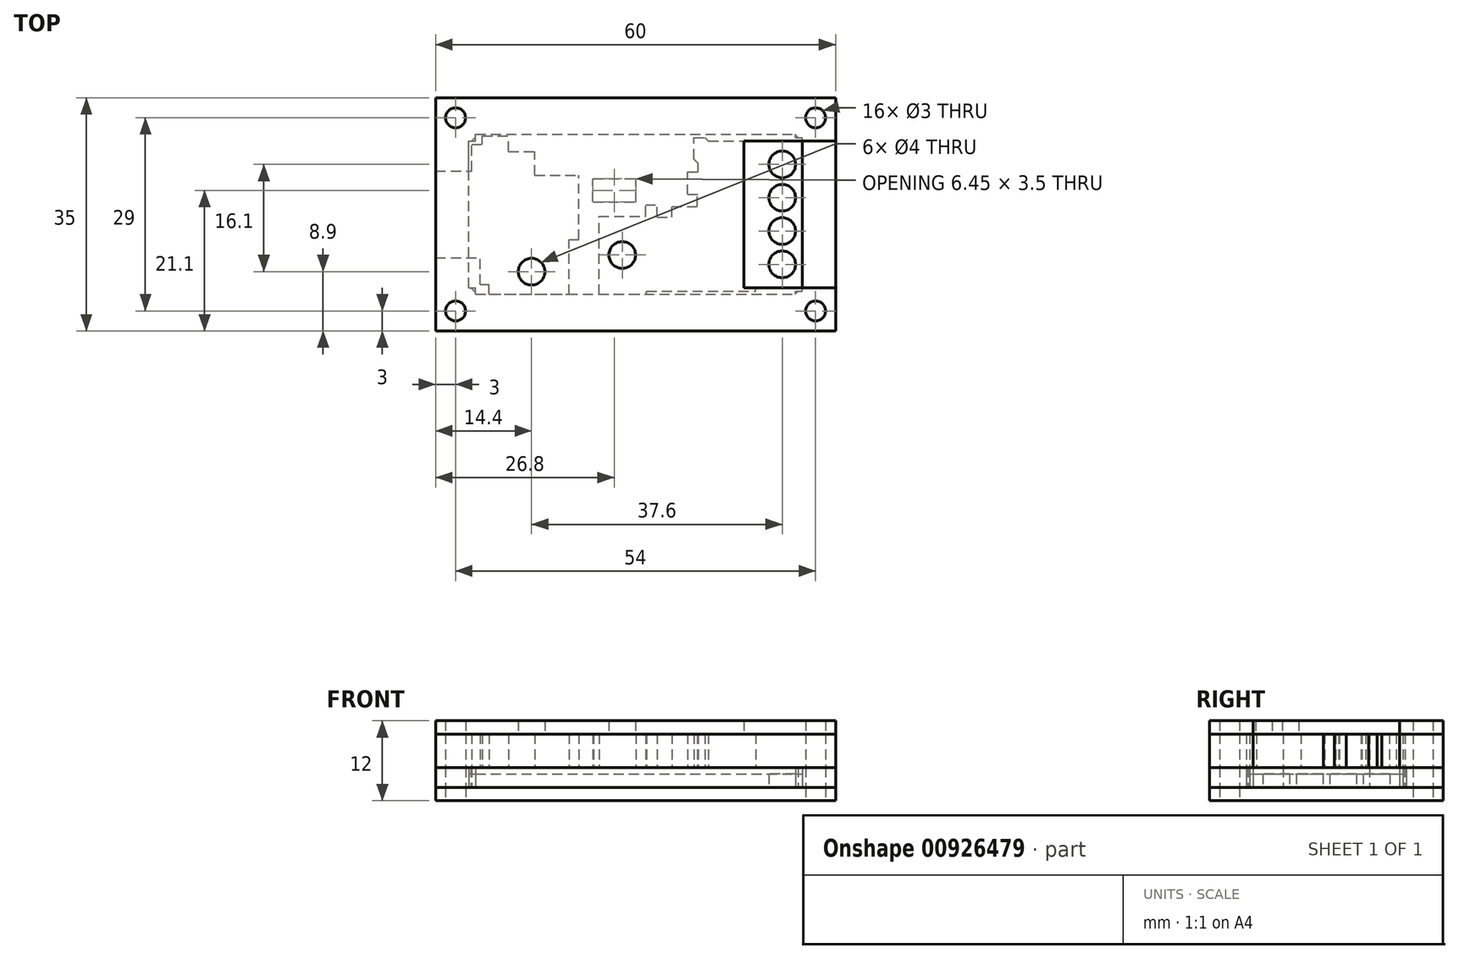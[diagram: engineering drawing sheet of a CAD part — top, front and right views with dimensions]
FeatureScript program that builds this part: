
annotation { "Feature Type Name" : "Feature", "Feature Type Description" : "" }
export const myFeature = defineFeature(function(context is Context, id is Id, definition is map)
    precondition{}
    {
        {
            var Q0;
            Q0=qCreatedBy(makeId("Top.planeOp"),FACE);
            var sketch = newSketch(context, id + "F0", { "sketchPlane" : qUnion([Q0])});
            skLineSegment(sketch, "E0", {"start": v(-30, -17.5) * mm, "end": v(-30, 17.5) * mm});
            skLineSegment(sketch, "E1", {"start": v(-30, 17.5) * mm, "end": v(30, 17.5) * mm});
            skLineSegment(sketch, "E2", {"start": v(30, -17.5) * mm, "end": v(30, 17.5) * mm});
            skLineSegment(sketch, "E3", {"start": v(-30, -17.5) * mm, "end": v(30, -17.5) * mm});
            skCircle(sketch, "E4", {"center": v(-27, -14.5) * mm, "radius": 1.5 * mm});
            skCircle(sketch, "E5", {"center": v(-27, 14.5) * mm, "radius": 1.5 * mm});
            skCircle(sketch, "E6", {"center": v(27, 14.5) * mm, "radius": 1.5 * mm});
            skCircle(sketch, "E7", {"center": v(27, -14.5) * mm, "radius": 1.5 * mm});
            skSolve(sketch);
        }
        {
            var Q0;
            Q0=makeQuery(id+"F0.imprint","IMPRINT",FACE,{"disambiguationData":[TD([[makeQuery(id+"F0.imprint","IMPRINT",EDGE,{"derivedFrom":sQuery(id+"F0.wireOp",EDGE,"E0")}),-1.0]])]});
            extrude(context, id + "F1", {"entities" : qUnion([Q0]), "depth" : 2 * mm, "offsetDistance" : 25 * mm});
        }
        {
            var Q0;
            Q0=makeQuery(id+"F1.opExtrude","CAP_FACE",FACE,{"disambiguationData":[OSD([sQuery(id+"F0.wireOp",EDGE,"E0"),sQuery(id+"F0.wireOp",EDGE,"E1"),sQuery(id+"F0.wireOp",EDGE,"E2"),sQuery(id+"F0.wireOp",EDGE,"E3"),sQuery(id+"F0.wireOp",EDGE,"E4"),sQuery(id+"F0.wireOp",EDGE,"E5"),sQuery(id+"F0.wireOp",EDGE,"E6"),sQuery(id+"F0.wireOp",EDGE,"E7")])],"isStart":false});
            cPlane(context, id + "F2", {"entities" : qUnion([Q0]), "cplaneType" : CPlaneType.OFFSET, "offset" : 0 * mm, "width" : 150 * mm, "height" : 150 * mm});
        }
        {
            var Q0;
            Q0=qCreatedBy(id+"F2.planeOp",FACE);
            var sketch = newSketch(context, id + "F3", { "sketchPlane" : qUnion([Q0])});
            skLineSegment(sketch, "E8", {"start": v(24, -12) * mm, "end": v(24, -11.9) * mm});
            skLineSegment(sketch, "E9", {"start": v(-25, -11) * mm, "end": v(-25, -6.5) * mm});
            skLineSegment(sketch, "E10", {"start": v(-30, -6.5) * mm, "end": v(-25, -6.5) * mm});
            skLineSegment(sketch, "E11", {"start": v(-30, 6.5) * mm, "end": v(-25, 6.5) * mm});
            skLineSegment(sketch, "E12", {"start": v(-25, 6.5) * mm, "end": v(-25, 11) * mm});
            skLineSegment(sketch, "E13", {"start": v(-24, 12) * mm, "end": v(24, 12) * mm});
            skLineSegment(sketch, "E14", {"start": v(25, -11.5) * mm, "end": v(25, 11.5) * mm});
            skLineSegment(sketch, "E15", {"start": v(-24, -12) * mm, "end": v(24, -12) * mm});
            skLineSegment(sketch, "E16", {"start": v(-30, -17.5) * mm, "end": v(-30, -6.5) * mm});
            skLineSegment(sketch, "E17", {"start": v(-30, -17.5) * mm, "end": v(30, -17.5) * mm});
            skLineSegment(sketch, "E18", {"start": v(30, -17.5) * mm, "end": v(30, 11) * mm});
            skLineSegment(sketch, "E19", {"start": v(30, 11) * mm, "end": v(30, 17.5) * mm});
            skLineSegment(sketch, "E20", {"start": v(-30, 17.5) * mm, "end": v(30, 17.5) * mm});
            skLineSegment(sketch, "E21", {"start": v(-30, 6.5) * mm, "end": v(-30, 17.5) * mm});
            skLineSegment(sketch, "E22", {"start": v(-25, 11) * mm, "end": v(-24.6, 11) * mm});
            skLineSegment(sketch, "E23", {"start": v(-24.6, 11) * mm, "end": v(-24, 11.6) * mm});
            skLineSegment(sketch, "E24", {"start": v(-24, 11.6) * mm, "end": v(-24, 12) * mm});
            skLineSegment(sketch, "E25", {"start": v(24.4, 11.5) * mm, "end": v(25, 11.5) * mm});
            skLineSegment(sketch, "E26", {"start": v(24, 11.9) * mm, "end": v(24.4, 11.5) * mm});
            skLineSegment(sketch, "E27", {"start": v(24, 11.9) * mm, "end": v(24, 12) * mm});
            skLineSegment(sketch, "E28", {"start": v(24.4, -11.5) * mm, "end": v(25, -11.5) * mm});
            skLineSegment(sketch, "E29", {"start": v(24, -11.9) * mm, "end": v(24.4, -11.5) * mm});
            skLineSegment(sketch, "E30", {"start": v(-24, -12) * mm, "end": v(-24, -11.7) * mm});
            skLineSegment(sketch, "E31", {"start": v(-24.7, -11) * mm, "end": v(-24, -11.7) * mm});
            skLineSegment(sketch, "E32", {"start": v(-25, -11) * mm, "end": v(-24.7, -11) * mm});
            skCircle(sketch, "E33", {"center": v(-27, -14.5) * mm, "radius": 1.5 * mm});
            skCircle(sketch, "E34", {"center": v(-27, 14.5) * mm, "radius": 1.5 * mm});
            skCircle(sketch, "E35", {"center": v(27, 14.5) * mm, "radius": 1.5 * mm});
            skCircle(sketch, "E36", {"center": v(27, -14.5) * mm, "radius": 1.5 * mm});
            skSolve(sketch);
        }
        {
            var Q0;
            Q0 = qSketchRegion(id + "F3", true);
            extrude(context, id + "F4", {"entities" : qUnion([Q0]), "depth" : 3 * mm, "offsetDistance" : 25 * mm});
        }
        {
            var Q0;
            Q0=qCreatedBy(id+"F2.planeOp",FACE);
            var sketch = newSketch(context, id + "F5", { "sketchPlane" : qUnion([Q0])});
            skLineSegment(sketch, "E37", {"start": v(-24, -12) * mm, "end": v(-24, -11) * mm});
            skLineSegment(sketch, "E38", {"start": v(-25, -11) * mm, "end": v(-24, -11) * mm});
            skLineSegment(sketch, "E39", {"start": v(-25, -11) * mm, "end": v(-25, 11) * mm});
            skLineSegment(sketch, "E40", {"start": v(-24, 12) * mm, "end": v(24, 12) * mm});
            skLineSegment(sketch, "E41", {"start": v(24, 11.5) * mm, "end": v(24, 12) * mm});
            skLineSegment(sketch, "E42", {"start": v(24, 11.5) * mm, "end": v(25, 11.5) * mm});
            skLineSegment(sketch, "E43", {"start": v(25, -11.5) * mm, "end": v(25, 11.5) * mm});
            skLineSegment(sketch, "E44", {"start": v(24, -11.5) * mm, "end": v(25, -11.5) * mm});
            skLineSegment(sketch, "E45", {"start": v(24, -12) * mm, "end": v(24, -11.5) * mm});
            skLineSegment(sketch, "E46", {"start": v(-24, -12) * mm, "end": v(24, -12) * mm});
            skLineSegment(sketch, "E47", {"start": v(-25, 11) * mm, "end": v(-24, 11) * mm});
            skLineSegment(sketch, "E48", {"start": v(-24, 11) * mm, "end": v(-24, 12) * mm});
            skCircle(sketch, "E49", {"center": v(22, 7.5) * mm, "radius": 2 * mm});
            skCircle(sketch, "E50", {"center": v(22, 2.5) * mm, "radius": 2 * mm});
            skCircle(sketch, "E51", {"center": v(22, -2.5) * mm, "radius": 2 * mm});
            skCircle(sketch, "E52", {"center": v(22, -7.5) * mm, "radius": 2 * mm});
            skSolve(sketch);
        }
        {
            var Q0;
            Q0 = qSketchRegion(id + "F5", true);
            extrude(context, id + "F6", {"entities" : qUnion([Q0]), "depth" : 2 * mm, "offsetDistance" : 25 * mm});
        }
        {
            var Q0;
            Q0=makeQuery(id+"F4.opExtrude","CAP_FACE",FACE,{"disambiguationData":[OSD([sQuery(id+"F3.wireOp",EDGE,"E8"),sQuery(id+"F3.wireOp",EDGE,"E9"),sQuery(id+"F3.wireOp",EDGE,"E10"),sQuery(id+"F3.wireOp",EDGE,"E11"),sQuery(id+"F3.wireOp",EDGE,"E12"),sQuery(id+"F3.wireOp",EDGE,"E13"),sQuery(id+"F3.wireOp",EDGE,"E14"),sQuery(id+"F3.wireOp",EDGE,"E15"),sQuery(id+"F3.wireOp",EDGE,"E16"),sQuery(id+"F3.wireOp",EDGE,"E17"),sQuery(id+"F3.wireOp",EDGE,"E18"),sQuery(id+"F3.wireOp",EDGE,"E19"),sQuery(id+"F3.wireOp",EDGE,"E20"),sQuery(id+"F3.wireOp",EDGE,"E21"),sQuery(id+"F3.wireOp",EDGE,"E22"),sQuery(id+"F3.wireOp",EDGE,"E23"),sQuery(id+"F3.wireOp",EDGE,"E24"),sQuery(id+"F3.wireOp",EDGE,"E25"),sQuery(id+"F3.wireOp",EDGE,"E26"),sQuery(id+"F3.wireOp",EDGE,"E27"),sQuery(id+"F3.wireOp",EDGE,"E28"),sQuery(id+"F3.wireOp",EDGE,"E29"),sQuery(id+"F3.wireOp",EDGE,"E30"),sQuery(id+"F3.wireOp",EDGE,"E31"),sQuery(id+"F3.wireOp",EDGE,"E32"),sQuery(id+"F3.wireOp",EDGE,"E33"),sQuery(id+"F3.wireOp",EDGE,"E34"),sQuery(id+"F3.wireOp",EDGE,"E35"),sQuery(id+"F3.wireOp",EDGE,"E36")])],"isStart":false});
            cPlane(context, id + "F7", {"entities" : qUnion([Q0]), "cplaneType" : CPlaneType.OFFSET, "offset" : 0 * mm, "width" : 150 * mm, "height" : 150 * mm});
        }
        {
            var Q0;
            Q0=qCreatedBy(id+"F7.planeOp",FACE);
            var sketch = newSketch(context, id + "F8", { "sketchPlane" : qUnion([Q0])});
            skLineSegment(sketch, "E53", {"start": v(-23, 11.8) * mm, "end": v(-19.05, 11.8) * mm});
            skLineSegment(sketch, "E54", {"start": v(-15.12, 5.9) * mm, "end": v(-8.5, 5.9) * mm});
            skLineSegment(sketch, "E55", {"start": v(-8.5, -1.5) * mm, "end": v(-8.5, 5.9) * mm});
            skLineSegment(sketch, "E56", {"start": v(-30, 6.5) * mm, "end": v(-30, 17.5) * mm});
            skLineSegment(sketch, "E57", {"start": v(-30, 17.5) * mm, "end": v(30, 17.5) * mm});
            skLineSegment(sketch, "E58", {"start": v(30, 11) * mm, "end": v(30, 17.5) * mm});
            skLineSegment(sketch, "E59", {"start": v(30, -17.5) * mm, "end": v(30, -11) * mm});
            skLineSegment(sketch, "E60", {"start": v(-30, -17.5) * mm, "end": v(30, -17.5) * mm});
            skLineSegment(sketch, "E61", {"start": v(-30, -17.5) * mm, "end": v(-30, -6.5) * mm});
            skLineSegment(sketch, "E62", {"start": v(-23.3, -10.5) * mm, "end": v(-23.3, -6.5) * mm});
            skLineSegment(sketch, "E63", {"start": v(-23.3, -10.5) * mm, "end": v(-22, -10.5) * mm});
            skLineSegment(sketch, "E64", {"start": v(-22, -12) * mm, "end": v(-22, -10.5) * mm});
            skLineSegment(sketch, "E65", {"start": v(-22, -12) * mm, "end": v(-10, -12) * mm});
            skLineSegment(sketch, "E66", {"start": v(-10, -12) * mm, "end": v(-10, -4.9) * mm});
            skLineSegment(sketch, "E67", {"start": v(-8.5, -3.78) * mm, "end": v(-8.5, -1.5) * mm});
            skLineSegment(sketch, "E68", {"start": v(2.75, -11.5) * mm, "end": v(10, -11.5) * mm});
            skLineSegment(sketch, "E69", {"start": v(10, -11.5) * mm, "end": v(15.5, -11.5) * mm});
            skLineSegment(sketch, "E70", {"start": v(15.5, -11.5) * mm, "end": v(18, -11.5) * mm});
            skLineSegment(sketch, "E71", {"start": v(18, -11.5) * mm, "end": v(18, -11) * mm});
            skLineSegment(sketch, "E72", {"start": v(18, -11) * mm, "end": v(30, -11) * mm});
            skLineSegment(sketch, "E73", {"start": v(17.2, 11) * mm, "end": v(30, 11) * mm});
            skLineSegment(sketch, "E74", {"start": v(-23, 10.5) * mm, "end": v(-23, 11.8) * mm});
            skLineSegment(sketch, "E75", {"start": v(-24.6, 10.5) * mm, "end": v(-23, 10.5) * mm});
            skLineSegment(sketch, "E76", {"start": v(-24.6, 6.5) * mm, "end": v(-24.6, 10.5) * mm});
            skLineSegment(sketch, "E77", {"start": v(-26, 6.5) * mm, "end": v(-24.6, 6.5) * mm});
            skLineSegment(sketch, "E78", {"start": v(-30, 6.5) * mm, "end": v(-26, 6.5) * mm});
            skLineSegment(sketch, "E79", {"start": v(-30, -6.5) * mm, "end": v(-23.3, -6.5) * mm});
            skLineSegment(sketch, "E80", {"start": v(-10, -4.9) * mm, "end": v(-10, -3.78) * mm});
            skLineSegment(sketch, "E81", {"start": v(-10, -3.78) * mm, "end": v(-8.5, -3.78) * mm});
            skLineSegment(sketch, "E82", {"start": v(0.02, 1.85) * mm, "end": v(0.02, 5.35) * mm});
            skLineSegment(sketch, "E83", {"start": v(-6.32, 1.85) * mm, "end": v(0.02, 1.85) * mm});
            skLineSegment(sketch, "E84", {"start": v(-6.42, 1.95) * mm, "end": v(-6.32, 1.85) * mm});
            skLineSegment(sketch, "E85", {"start": v(-6.42, 1.95) * mm, "end": v(-6.42, 5.2) * mm});
            skLineSegment(sketch, "E86", {"start": v(-6.42, 5.2) * mm, "end": v(-6.27, 5.35) * mm});
            skLineSegment(sketch, "E87", {"start": v(-6.27, 5.35) * mm, "end": v(0.02, 5.35) * mm});
            skLineSegment(sketch, "E88", {"start": v(1.65, -11.5) * mm, "end": v(2.75, -11.5) * mm});
            skLineSegment(sketch, "E89", {"start": v(-5.5, -12) * mm, "end": v(1.4, -12) * mm});
            skLineSegment(sketch, "E90", {"start": v(-5.5, -12) * mm, "end": v(-5.5, -0.95) * mm});
            skLineSegment(sketch, "E91", {"start": v(-5.5, -0.95) * mm, "end": v(-5.5, -0.28) * mm});
            skLineSegment(sketch, "E92", {"start": v(-5.5, -0.28) * mm, "end": v(1.5, -0.28) * mm});
            skLineSegment(sketch, "E93", {"start": v(1.5, -0.28) * mm, "end": v(1.5, 1.4) * mm});
            skLineSegment(sketch, "E94", {"start": v(1.5, 1.4) * mm, "end": v(3.23, 1.4) * mm});
            skLineSegment(sketch, "E95", {"start": v(3.23, -0.43) * mm, "end": v(3.23, 1.4) * mm});
            skLineSegment(sketch, "E96", {"start": v(3.23, -0.43) * mm, "end": v(5.42, -0.43) * mm});
            skLineSegment(sketch, "E97", {"start": v(5.42, -0.43) * mm, "end": v(5.42, 1.2) * mm});
            skLineSegment(sketch, "E98", {"start": v(5.65, 1.2) * mm, "end": v(9.27, 1.2) * mm});
            skLineSegment(sketch, "E99", {"start": v(9.27, 1.2) * mm, "end": v(9.27, 2.97) * mm});
            skLineSegment(sketch, "E100", {"start": v(9.25, 3) * mm, "end": v(9.27, 2.97) * mm});
            skLineSegment(sketch, "E101", {"start": v(7.82, 3) * mm, "end": v(9.25, 3) * mm});
            skLineSegment(sketch, "E102", {"start": v(7.82, 3) * mm, "end": v(7.82, 6.37) * mm});
            skLineSegment(sketch, "E103", {"start": v(7.82, 6.37) * mm, "end": v(9.4, 6.37) * mm});
            skLineSegment(sketch, "E104", {"start": v(9.4, 6.37) * mm, "end": v(9.4, 7.65) * mm});
            skLineSegment(sketch, "E105", {"start": v(-19.05, 9.45) * mm, "end": v(-19.05, 11.8) * mm});
            skLineSegment(sketch, "E106", {"start": v(-19.05, 9.45) * mm, "end": v(-15.12, 9.45) * mm});
            skLineSegment(sketch, "E107", {"start": v(-15.12, 5.9) * mm, "end": v(-15.12, 9.45) * mm});
            skLineSegment(sketch, "E108", {"start": v(8.75, 11.5) * mm, "end": v(10.42, 11.5) * mm});
            skLineSegment(sketch, "E109", {"start": v(8.75, 8.3) * mm, "end": v(8.75, 11.5) * mm});
            skLineSegment(sketch, "E110", {"start": v(8.75, 8.3) * mm, "end": v(9.4, 7.65) * mm});
            skLineSegment(sketch, "E111", {"start": v(10.92, 11) * mm, "end": v(17.2, 11) * mm});
            skLineSegment(sketch, "E112", {"start": v(5.42, 1.2) * mm, "end": v(5.65, 1.2) * mm});
            skLineSegment(sketch, "E113", {"start": v(10.42, 11.5) * mm, "end": v(10.92, 11) * mm});
            skLineSegment(sketch, "E114", {"start": v(1.4, -12) * mm, "end": v(1.65, -12) * mm});
            skLineSegment(sketch, "E115", {"start": v(1.65, -12) * mm, "end": v(1.65, -11.5) * mm});
            skCircle(sketch, "E116", {"center": v(-27, -14.5) * mm, "radius": 1.5 * mm});
            skCircle(sketch, "E117", {"center": v(-27, 14.5) * mm, "radius": 1.5 * mm});
            skCircle(sketch, "E118", {"center": v(27, 14.5) * mm, "radius": 1.5 * mm});
            skCircle(sketch, "E119", {"center": v(27, -14.5) * mm, "radius": 1.5 * mm});
            skSolve(sketch);
        }
        {
            var Q0;
            Q0 = qSketchRegion(id + "F8", true);
            extrude(context, id + "F9", {"entities" : qUnion([Q0]), "depth" : 5 * mm, "offsetDistance" : 25 * mm});
        }
        {
            var Q0;
            Q0=makeQuery(id+"F9.opExtrude","CAP_FACE",FACE,{"disambiguationData":[OSD([sQuery(id+"F8.wireOp",EDGE,"E53"),sQuery(id+"F8.wireOp",EDGE,"E54"),sQuery(id+"F8.wireOp",EDGE,"E55"),sQuery(id+"F8.wireOp",EDGE,"E56"),sQuery(id+"F8.wireOp",EDGE,"E57"),sQuery(id+"F8.wireOp",EDGE,"E58"),sQuery(id+"F8.wireOp",EDGE,"E59"),sQuery(id+"F8.wireOp",EDGE,"E60"),sQuery(id+"F8.wireOp",EDGE,"E61"),sQuery(id+"F8.wireOp",EDGE,"E62"),sQuery(id+"F8.wireOp",EDGE,"E63"),sQuery(id+"F8.wireOp",EDGE,"E64"),sQuery(id+"F8.wireOp",EDGE,"E65"),sQuery(id+"F8.wireOp",EDGE,"E66"),sQuery(id+"F8.wireOp",EDGE,"E67"),sQuery(id+"F8.wireOp",EDGE,"E68"),sQuery(id+"F8.wireOp",EDGE,"E69"),sQuery(id+"F8.wireOp",EDGE,"E70"),sQuery(id+"F8.wireOp",EDGE,"E71"),sQuery(id+"F8.wireOp",EDGE,"E72"),sQuery(id+"F8.wireOp",EDGE,"E73"),sQuery(id+"F8.wireOp",EDGE,"E74"),sQuery(id+"F8.wireOp",EDGE,"E75"),sQuery(id+"F8.wireOp",EDGE,"E76"),sQuery(id+"F8.wireOp",EDGE,"E77"),sQuery(id+"F8.wireOp",EDGE,"E78"),sQuery(id+"F8.wireOp",EDGE,"E79"),sQuery(id+"F8.wireOp",EDGE,"E80"),sQuery(id+"F8.wireOp",EDGE,"E81"),sQuery(id+"F8.wireOp",EDGE,"E82"),sQuery(id+"F8.wireOp",EDGE,"E83"),sQuery(id+"F8.wireOp",EDGE,"E84"),sQuery(id+"F8.wireOp",EDGE,"E85"),sQuery(id+"F8.wireOp",EDGE,"E86"),sQuery(id+"F8.wireOp",EDGE,"E87"),sQuery(id+"F8.wireOp",EDGE,"E88"),sQuery(id+"F8.wireOp",EDGE,"E89"),sQuery(id+"F8.wireOp",EDGE,"E90"),sQuery(id+"F8.wireOp",EDGE,"E91"),sQuery(id+"F8.wireOp",EDGE,"E92"),sQuery(id+"F8.wireOp",EDGE,"E93"),sQuery(id+"F8.wireOp",EDGE,"E94"),sQuery(id+"F8.wireOp",EDGE,"E95"),sQuery(id+"F8.wireOp",EDGE,"E96"),sQuery(id+"F8.wireOp",EDGE,"E97"),sQuery(id+"F8.wireOp",EDGE,"E98"),sQuery(id+"F8.wireOp",EDGE,"E99"),sQuery(id+"F8.wireOp",EDGE,"E100"),sQuery(id+"F8.wireOp",EDGE,"E101"),sQuery(id+"F8.wireOp",EDGE,"E102"),sQuery(id+"F8.wireOp",EDGE,"E103"),sQuery(id+"F8.wireOp",EDGE,"E104"),sQuery(id+"F8.wireOp",EDGE,"E105"),sQuery(id+"F8.wireOp",EDGE,"E106"),sQuery(id+"F8.wireOp",EDGE,"E107"),sQuery(id+"F8.wireOp",EDGE,"E108"),sQuery(id+"F8.wireOp",EDGE,"E109"),sQuery(id+"F8.wireOp",EDGE,"E110"),sQuery(id+"F8.wireOp",EDGE,"E111"),sQuery(id+"F8.wireOp",EDGE,"E112"),sQuery(id+"F8.wireOp",EDGE,"E113"),sQuery(id+"F8.wireOp",EDGE,"E114"),sQuery(id+"F8.wireOp",EDGE,"E115"),sQuery(id+"F8.wireOp",EDGE,"E116"),sQuery(id+"F8.wireOp",EDGE,"E117"),sQuery(id+"F8.wireOp",EDGE,"E118"),sQuery(id+"F8.wireOp",EDGE,"E119")])],"isStart":false});
            cPlane(context, id + "F10", {"entities" : qUnion([Q0]), "cplaneType" : CPlaneType.OFFSET, "offset" : 0 * mm, "width" : 150 * mm, "height" : 150 * mm});
        }
        {
            var Q0;
            Q0=qCreatedBy(id+"F10.planeOp",FACE);
            var sketch = newSketch(context, id + "F11", { "sketchPlane" : qUnion([Q0])});
            skLineSegment(sketch, "E120", {"start": v(-30, -17.5) * mm, "end": v(30, -17.5) * mm});
            skLineSegment(sketch, "E121", {"start": v(30, -17.5) * mm, "end": v(30, -11) * mm});
            skLineSegment(sketch, "E122", {"start": v(16.25, -11) * mm, "end": v(30, -11) * mm});
            skLineSegment(sketch, "E123", {"start": v(16.25, -11) * mm, "end": v(16.25, 11) * mm});
            skLineSegment(sketch, "E124", {"start": v(16.25, 11) * mm, "end": v(30, 11) * mm});
            skLineSegment(sketch, "E125", {"start": v(30, 11) * mm, "end": v(30, 17.5) * mm});
            skLineSegment(sketch, "E126", {"start": v(-30, -17.5) * mm, "end": v(-30, 17.5) * mm});
            skLineSegment(sketch, "E127", {"start": v(-30, 17.5) * mm, "end": v(30, 17.5) * mm});
            skCircle(sketch, "E128", {"center": v(-15.6, -8.6) * mm, "radius": 2 * mm});
            skCircle(sketch, "E129", {"center": v(-2, -6.1) * mm, "radius": 2 * mm});
            skCircle(sketch, "E130", {"center": v(-27, -14.5) * mm, "radius": 1.5 * mm});
            skCircle(sketch, "E131", {"center": v(-27, 14.5) * mm, "radius": 1.5 * mm});
            skCircle(sketch, "E132", {"center": v(27, 14.5) * mm, "radius": 1.5 * mm});
            skCircle(sketch, "E133", {"center": v(27, -14.5) * mm, "radius": 1.5 * mm});
            skSolve(sketch);
        }
        {
            var Q0;
            Q0=makeQuery(id+"F11.imprint","IMPRINT",FACE,{"disambiguationData":[TD([[makeQuery(id+"F11.imprint","IMPRINT",EDGE,{"derivedFrom":sQuery(id+"F11.wireOp",EDGE,"E120")}),1.0]])]});
            extrude(context, id + "F12", {"entities" : qUnion([Q0]), "depth" : 2 * mm, "offsetDistance" : 25 * mm});
        }
    });
